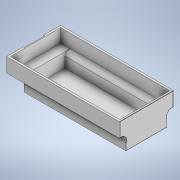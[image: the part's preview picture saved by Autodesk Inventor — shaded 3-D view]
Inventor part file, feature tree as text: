
AUTODESK INVENTOR PART (.ipt)
format: ipt  version: 2020.1 (Build 241239000, 239)  size: 278,016 bytes
history: native  units: mm
features: extrude x11, sketch x11, projected_geometry x9, other x1, fillet x1, shell x1
ambient origin geometry x8: Origin, YZ Plane, XZ Plane, XY Plane, X Axis, Y Axis, Z Axis, Center Point
bodies: Body1 (feature_tree)
feature tree (34):
  other  "Твердое тело1"
  extrude  "Выдавливание1"  Depth=142.0mm
  fillet  "Сопряжение1"  Radius=190.0mm
  extrude  "Выдавливание2"  Depth=50.0mm
  shell  "Оболочка1"  Thickness=24.0mm
  sketch  "Эскиз3"
  sketch  "Эскиз4"
  extrude  "Выдавливание3"  Depth=24.0mm
  extrude  "Выдавливание4"  Depth=50.0mm
  extrude  "Выдавливание5"  Depth=355.0mm TaperAngle=0.0deg
  sketch  "Эскиз6"
  sketch  "Эскиз7"
  extrude  "Выдавливание6"  Depth=18.0mm
  extrude  "Выдавливание7"  Depth=35.0mm TaperAngle=0.0deg
  extrude  "Выдавливание8"  Depth=3.0mm
  extrude  "Выдавливание9"  Depth=1.5mm TaperAngle=0.0deg
  extrude  "Выдавливание10"  Depth=1.5mm TaperAngle=0.0deg
  extrude  "Выдавливание11"  Depth=2.0mm TaperAngle=0.0deg
  sketch  "Эскиз1"
  sketch  "Эскиз2"
  projected_geometry  "Спроецированная петля1"
  projected_geometry  "Спроецированная петля2"
  projected_geometry  "Спроецированная петля3"
  projected_geometry  "Спроецированная петля4"
  sketch  "Эскиз5"
  projected_geometry  "Спроецированная петля5"
  projected_geometry  "Спроецированная петля6"
  projected_geometry  "Спроецированная петля7"
  sketch  "Эскиз8"
  sketch  "Эскиз9"
  sketch  "Эскиз10"
  projected_geometry  "Спроецированная петля8"
  sketch  "Эскиз11"
  projected_geometry  "Спроецированная петля9"
